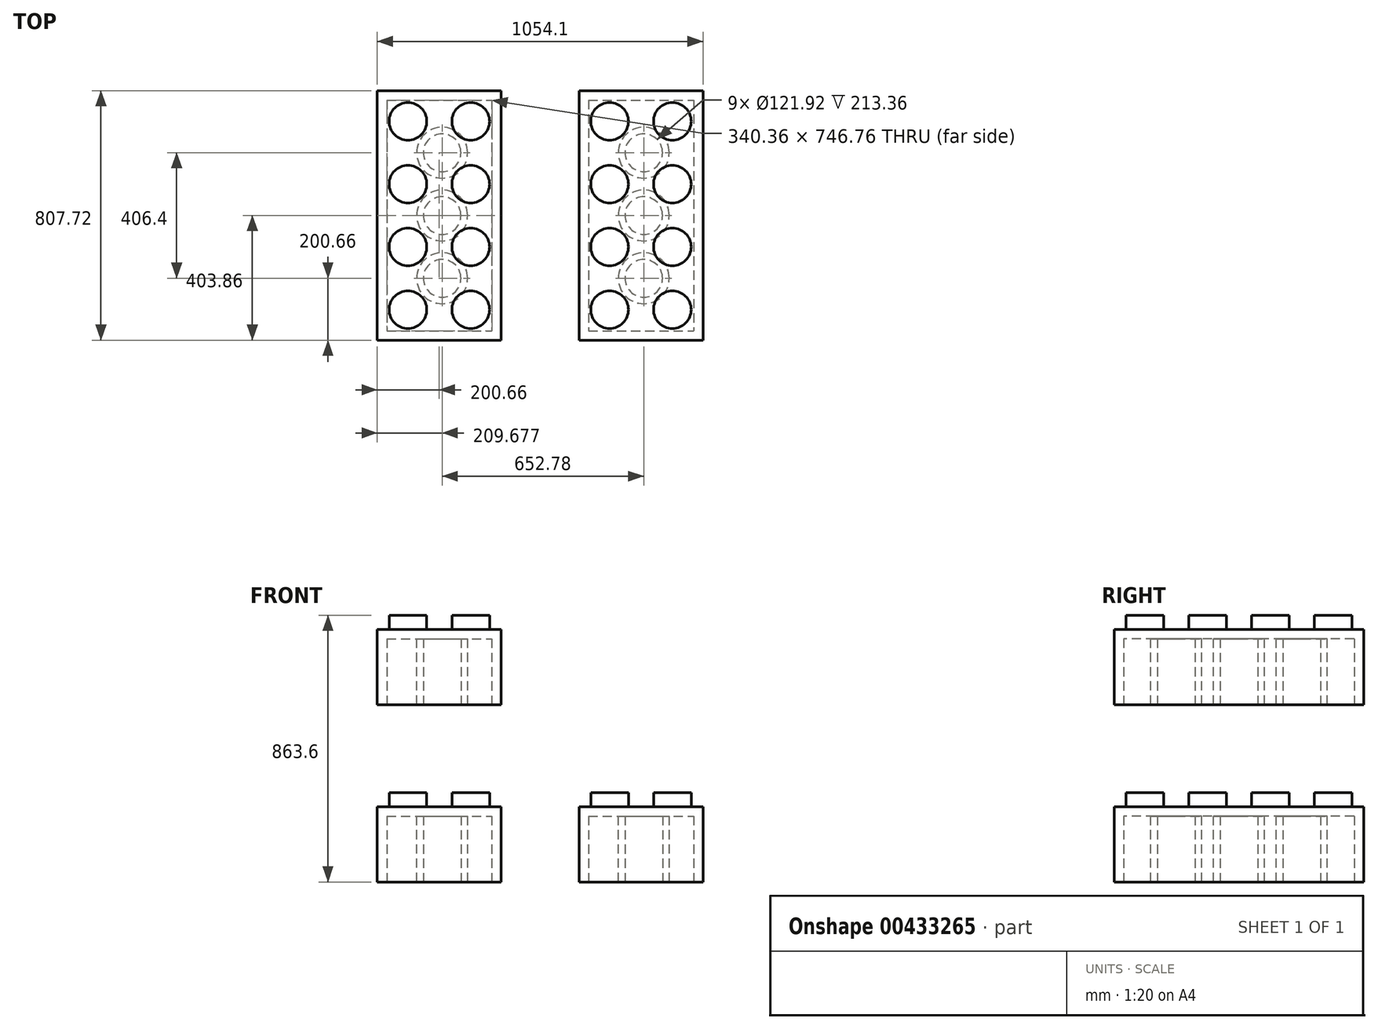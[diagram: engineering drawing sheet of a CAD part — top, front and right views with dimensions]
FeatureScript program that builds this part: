
annotation { "Feature Type Name" : "Feature", "Feature Type Description" : "" }
export const myFeature = defineFeature(function(context is Context, id is Id, definition is map)
    precondition{}
    {
        {
            var Q0;
            Q0=qCreatedBy(makeId("Top.planeOp"),FACE);
            var sketch = newSketch(context, id + "F0", { "sketchPlane" : qUnion([Q0])});
            skLineSegment(sketch, "E0.bottom", {"start": v(-200.66, 403.86) * mm, "end": v(200.66, 403.86) * mm});
            skLineSegment(sketch, "E0.top", {"start": v(-200.66, -403.86) * mm, "end": v(200.66, -403.86) * mm});
            skLineSegment(sketch, "E0.left", {"start": v(-200.66, 403.86) * mm, "end": v(-200.66, -403.86) * mm});
            skLineSegment(sketch, "E0.right", {"start": v(200.66, 403.86) * mm, "end": v(200.66, -403.86) * mm});
            skPoint(sketch, "E0.middle", {"position": v(0, 0) * mm});
            skSolve(sketch);
        }
        {
            var Q0;
            Q0=makeQuery(id+"F0.imprint","IMPRINT",FACE,{"disambiguationData":[TD([[makeQuery(id+"F0.imprint","IMPRINT",EDGE,{"derivedFrom":sQuery(id+"F0.wireOp",EDGE,"E0.bottom")}),-1.0]])]});
            extrude(context, id + "F1", {"entities" : qUnion([Q0]), "depth" : 243.84 * mm});
        }
        {
            var Q0;
            Q0=makeQuery(id+"F1.opExtrude","CAP_FACE",FACE,{"disambiguationData":[OSD([sQuery(id+"F0.wireOp",EDGE,"E0.bottom"),sQuery(id+"F0.wireOp",EDGE,"E0.top"),sQuery(id+"F0.wireOp",EDGE,"E0.left"),sQuery(id+"F0.wireOp",EDGE,"E0.right")])],"isStart":false});
            var sketch = newSketch(context, id + "F2", { "sketchPlane" : qUnion([Q0])});
            skCircle(sketch, "E1", {"center": v(-101.6, 304.8) * mm, "radius": 60.96 * mm});
            skCircle(sketch, "E2.0.1.0", {"center": v(-101.6, 101.6) * mm, "radius": 60.96 * mm});
            skCircle(sketch, "E2.0.2.0", {"center": v(-101.6, -101.6) * mm, "radius": 60.96 * mm});
            skCircle(sketch, "E2.0.3.0", {"center": v(-101.6, -304.8) * mm, "radius": 60.96 * mm});
            skCircle(sketch, "E2.1.0.0", {"center": v(101.6, 304.8) * mm, "radius": 60.96 * mm});
            skCircle(sketch, "E2.1.1.0", {"center": v(101.6, 101.6) * mm, "radius": 60.96 * mm});
            skCircle(sketch, "E2.1.2.0", {"center": v(101.6, -101.6) * mm, "radius": 60.96 * mm});
            skCircle(sketch, "E2.1.3.0", {"center": v(101.6, -304.8) * mm, "radius": 60.96 * mm});
            skLineSegment(sketch, "E2.direction1", {"start": v(-101.6, 304.8) * mm, "end": v(101.6, 304.8) * mm, "construction": true});
            skLineSegment(sketch, "E2.direction2", {"start": v(-101.6, 304.8) * mm, "end": v(-101.6, 101.6) * mm, "construction": true});
            skSolve(sketch);
        }
        {
            var Q0;
            Q0=makeQuery(id+"F2.imprint","IMPRINT",FACE,{"disambiguationData":[TD([[makeQuery(id+"F2.imprint","IMPRINT",EDGE,{"derivedFrom":sQuery(id+"F2.wireOp",EDGE,"E1")}),1.0]])]});
            var Q1;
            Q1=makeQuery(id+"F2.imprint","IMPRINT",FACE,{"disambiguationData":[TD([[makeQuery(id+"F2.imprint","IMPRINT",EDGE,{"derivedFrom":sQuery(id+"F2.wireOp",EDGE,"E2.1.0.0")}),1.0]])]});
            var Q2;
            Q2=makeQuery(id+"F2.imprint","IMPRINT",FACE,{"disambiguationData":[TD([[makeQuery(id+"F2.imprint","IMPRINT",EDGE,{"derivedFrom":sQuery(id+"F2.wireOp",EDGE,"E2.0.1.0")}),1.0]])]});
            var Q3;
            Q3=makeQuery(id+"F2.imprint","IMPRINT",FACE,{"disambiguationData":[TD([[makeQuery(id+"F2.imprint","IMPRINT",EDGE,{"derivedFrom":sQuery(id+"F2.wireOp",EDGE,"E2.1.1.0")}),1.0]])]});
            var Q4;
            Q4=makeQuery(id+"F2.imprint","IMPRINT",FACE,{"disambiguationData":[TD([[makeQuery(id+"F2.imprint","IMPRINT",EDGE,{"derivedFrom":sQuery(id+"F2.wireOp",EDGE,"E2.0.2.0")}),1.0]])]});
            var Q5;
            Q5=makeQuery(id+"F2.imprint","IMPRINT",FACE,{"disambiguationData":[TD([[makeQuery(id+"F2.imprint","IMPRINT",EDGE,{"derivedFrom":sQuery(id+"F2.wireOp",EDGE,"E2.1.2.0")}),1.0]])]});
            var Q6;
            Q6=makeQuery(id+"F2.imprint","IMPRINT",FACE,{"disambiguationData":[TD([[makeQuery(id+"F2.imprint","IMPRINT",EDGE,{"derivedFrom":sQuery(id+"F2.wireOp",EDGE,"E2.0.3.0")}),1.0]])]});
            var Q7;
            Q7=makeQuery(id+"F2.imprint","IMPRINT",FACE,{"disambiguationData":[TD([[makeQuery(id+"F2.imprint","IMPRINT",EDGE,{"derivedFrom":sQuery(id+"F2.wireOp",EDGE,"E2.1.3.0")}),1.0]])]});
            extrude(context, id + "F3", {"entities" : qUnion([Q0, Q1, Q2, Q3, Q4, Q5, Q6, Q7]), "operationType" : NewBodyOperationType.ADD, "depth" : 45.72 * mm});
        }
        {
            var Q0;
            Q0=makeQuery(id+"F1.opExtrude","CAP_FACE",FACE,{"disambiguationData":[OSD([sQuery(id+"F0.wireOp",EDGE,"E0.bottom"),sQuery(id+"F0.wireOp",EDGE,"E0.top"),sQuery(id+"F0.wireOp",EDGE,"E0.left"),sQuery(id+"F0.wireOp",EDGE,"E0.right")])],"isStart":true});
            var sketch = newSketch(context, id + "F4", { "sketchPlane" : qUnion([Q0])});
            skLineSegment(sketch, "E3.bottom", {"start": v(-170.18, -373.38) * mm, "end": v(170.18, -373.38) * mm});
            skLineSegment(sketch, "E3.top", {"start": v(-170.18, 373.38) * mm, "end": v(170.18, 373.38) * mm});
            skLineSegment(sketch, "E3.left", {"start": v(-170.18, -373.38) * mm, "end": v(-170.18, 373.38) * mm});
            skLineSegment(sketch, "E3.right", {"start": v(170.18, -373.38) * mm, "end": v(170.18, 373.38) * mm});
            skPoint(sketch, "E3.middle", {"position": v(0, 0) * mm});
            skSolve(sketch);
        }
        {
            var Q0;
            Q0=makeQuery(id+"F4.imprint","IMPRINT",FACE,{"disambiguationData":[TD([[makeQuery(id+"F4.imprint","IMPRINT",EDGE,{"derivedFrom":sQuery(id+"F4.wireOp",EDGE,"E3.bottom")}),1.0]])]});
            extrude(context, id + "F5", {"entities" : qUnion([Q0]), "operationType" : NewBodyOperationType.REMOVE, "oppositeDirection" : true, "depth" : 213.36 * mm});
        }
        {
            var Q0;
            Q0=makeQuery(id+"F5.boolean.opBoolean","COPY",FACE,{"derivedFrom":makeQuery(id+"F5.opExtrude","CAP_FACE",FACE,{"disambiguationData":[OSD([sQuery(id+"F4.wireOp",EDGE,"E3.bottom"),sQuery(id+"F4.wireOp",EDGE,"E3.top"),sQuery(id+"F4.wireOp",EDGE,"E3.left"),sQuery(id+"F4.wireOp",EDGE,"E3.right")])],"isStart":false})});
            var sketch = newSketch(context, id + "F6", { "sketchPlane" : qUnion([Q0])});
            skCircle(sketch, "E4", {"center": v(9.02, 0) * mm, "radius": 82.55 * mm});
            skCircle(sketch, "E5.0.1.0", {"center": v(9.02, 203.2) * mm, "radius": 82.55 * mm});
            skLineSegment(sketch, "E5.direction1", {"start": v(9.02, 0) * mm, "end": v(301.12, 0) * mm, "construction": true});
            skLineSegment(sketch, "E5.direction2", {"start": v(9.02, 0) * mm, "end": v(9.02, 203.2) * mm, "construction": true});
            skCircle(sketch, "E6.0.1.0", {"center": v(9.02, -203.2) * mm, "radius": 82.55 * mm});
            skLineSegment(sketch, "E6.direction1", {"start": v(9.02, 0) * mm, "end": v(237.62, 0) * mm, "construction": true});
            skLineSegment(sketch, "E6.direction2", {"start": v(9.02, 0) * mm, "end": v(9.02, -203.2) * mm, "construction": true});
            skSolve(sketch);
        }
        {
            var Q0;
            Q0=makeQuery(id+"F6.imprint","IMPRINT",FACE,{"disambiguationData":[TD([[makeQuery(id+"F6.imprint","IMPRINT",EDGE,{"derivedFrom":sQuery(id+"F6.wireOp",EDGE,"E6.0.1.0")}),1.0]])]});
            var Q1;
            Q1=makeQuery(id+"F6.imprint","IMPRINT",FACE,{"disambiguationData":[TD([[makeQuery(id+"F6.imprint","IMPRINT",EDGE,{"derivedFrom":sQuery(id+"F6.wireOp",EDGE,"E4")}),1.0]])]});
            var Q2;
            Q2=makeQuery(id+"F6.imprint","IMPRINT",FACE,{"disambiguationData":[TD([[makeQuery(id+"F6.imprint","IMPRINT",EDGE,{"derivedFrom":sQuery(id+"F6.wireOp",EDGE,"E5.0.1.0")}),1.0]])]});
            extrude(context, id + "F7", {"entities" : qUnion([Q0, Q1, Q2]), "operationType" : NewBodyOperationType.ADD, "depth" : 213.36 * mm});
        }
        {
            var Q0;
            Q0=makeQuery(id+"F7.opExtrude","CAP_FACE",FACE,{"disambiguationData":[OSD([sQuery(id+"F6.wireOp",EDGE,"E4")])],"isStart":false});
            var sketch = newSketch(context, id + "F8", { "sketchPlane" : qUnion([Q0])});
            skCircle(sketch, "E7", {"center": v(9.02, 0) * mm, "radius": 60.96 * mm});
            skCircle(sketch, "E8.0.1.0", {"center": v(9.02, 203.2) * mm, "radius": 60.96 * mm});
            skLineSegment(sketch, "E8.direction1", {"start": v(9.02, 0) * mm, "end": v(34.42, 0) * mm, "construction": true});
            skLineSegment(sketch, "E8.direction2", {"start": v(9.02, 0) * mm, "end": v(9.02, 203.2) * mm, "construction": true});
            skCircle(sketch, "E9.0.1.0", {"center": v(9.02, -203.2) * mm, "radius": 60.96 * mm});
            skLineSegment(sketch, "E9.direction1", {"start": v(9.02, 0) * mm, "end": v(318.9, 0) * mm, "construction": true});
            skLineSegment(sketch, "E9.direction2", {"start": v(9.02, 0) * mm, "end": v(9.02, -203.2) * mm, "construction": true});
            skSolve(sketch);
        }
        {
            var Q0;
            Q0=makeQuery(id+"F8.imprint","IMPRINT",FACE,{"disambiguationData":[TD([[makeQuery(id+"F8.imprint","IMPRINT",EDGE,{"derivedFrom":sQuery(id+"F8.wireOp",EDGE,"E8.0.1.0")}),1.0]])]});
            var Q1;
            Q1=makeQuery(id+"F8.imprint","IMPRINT",FACE,{"disambiguationData":[TD([[makeQuery(id+"F8.imprint","IMPRINT",EDGE,{"derivedFrom":sQuery(id+"F8.wireOp",EDGE,"E7")}),1.0]])]});
            var Q2;
            Q2=makeQuery(id+"F8.imprint","IMPRINT",FACE,{"disambiguationData":[TD([[makeQuery(id+"F8.imprint","IMPRINT",EDGE,{"derivedFrom":sQuery(id+"F8.wireOp",EDGE,"E9.0.1.0")}),1.0]])]});
            extrude(context, id + "F9", {"entities" : qUnion([Q0, Q1, Q2]), "operationType" : NewBodyOperationType.REMOVE, "oppositeDirection" : true, "depth" : 213.36 * mm});
        }
        {
            var Q0;
            Q0=makeQuery(id+"F1.opExtrude","SWEPT_BODY",BODY,{"disambiguationData":[OSD([sQuery(id+"F0.wireOp",EDGE,"E0.bottom"),sQuery(id+"F0.wireOp",EDGE,"E0.top"),sQuery(id+"F0.wireOp",EDGE,"E0.left"),sQuery(id+"F0.wireOp",EDGE,"E0.right")])]});
            transform(context, id + "F10", {"entities" : qUnion([Q0]), "transformType" : TransformType.TRANSLATION_3D, "dx" : 0 * mm, "dy" : 0 * mm, "dz" : 574.04 * mm, "makeCopy" : true});
        }
        {
            var Q0;
            Q0=makeQuery(id+"F1.opExtrude","SWEPT_BODY",BODY,{"disambiguationData":[OSD([sQuery(id+"F0.wireOp",EDGE,"E0.bottom"),sQuery(id+"F0.wireOp",EDGE,"E0.top"),sQuery(id+"F0.wireOp",EDGE,"E0.left"),sQuery(id+"F0.wireOp",EDGE,"E0.right")])]});
            transform(context, id + "F11", {"entities" : qUnion([Q0]), "transformType" : TransformType.TRANSLATION_3D, "dx" : 652.78 * mm, "dy" : 0 * mm, "dz" : 0 * mm, "makeCopy" : true});
        }
    });
